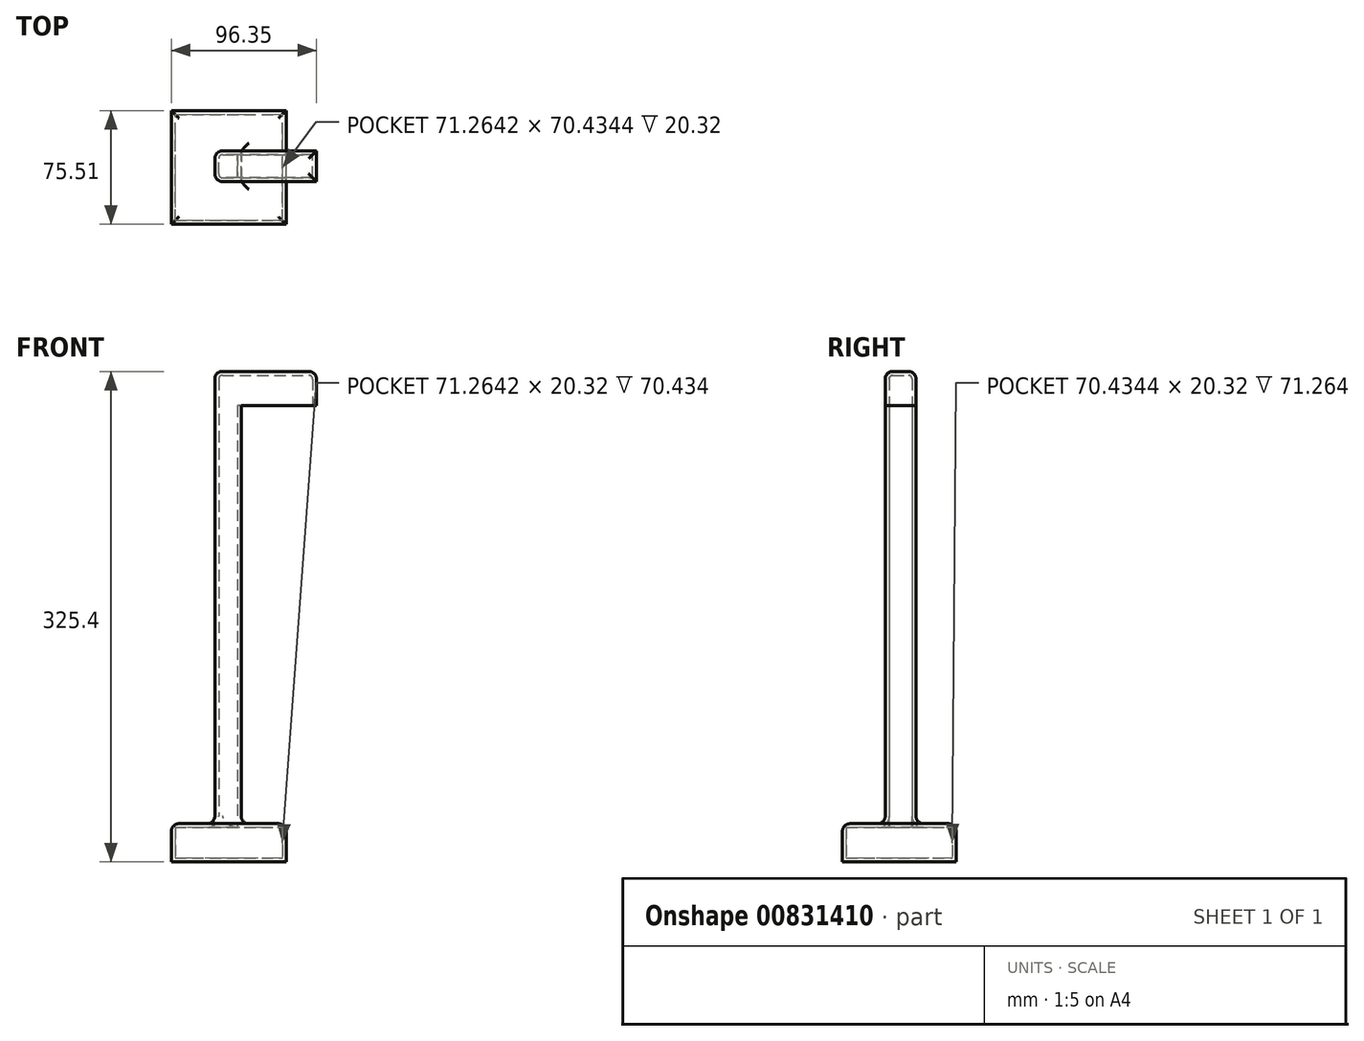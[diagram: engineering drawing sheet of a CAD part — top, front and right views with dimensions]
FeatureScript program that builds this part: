
annotation { "Feature Type Name" : "Feature", "Feature Type Description" : "" }
export const myFeature = defineFeature(function(context is Context, id is Id, definition is map)
    precondition{}
    {
        {
            var Q0;
            Q0=qCreatedBy(makeId("Top.planeOp"),FACE);
            var sketch = newSketch(context, id + "F0", { "sketchPlane" : qUnion([Q0])});
            skLineSegment(sketch, "E0.bottom", {"start": v(0, 0) * mm, "end": v(76.34, 0) * mm});
            skLineSegment(sketch, "E0.top", {"start": v(0, 75.51) * mm, "end": v(76.34, 75.51) * mm});
            skLineSegment(sketch, "E0.left", {"start": v(0, 0) * mm, "end": v(0, 75.51) * mm});
            skLineSegment(sketch, "E0.right", {"start": v(76.34, 0) * mm, "end": v(76.34, 75.51) * mm});
            skSolve(sketch);
        }
        {
            var Q0;
            Q0 = qSketchRegion(id + "F0", true);
            extrude(context, id + "F1", {"entities" : qUnion([Q0]), "depth" : 25.4 * mm, "offsetDistance" : 25.4 * mm});
        }
        {
            var Q0;
            Q0=makeQuery(id+"F1.opExtrude","CAP_FACE",FACE,{"disambiguationData":[OSD([sQuery(id+"F0.wireOp",EDGE,"E0.bottom"),sQuery(id+"F0.wireOp",EDGE,"E0.top"),sQuery(id+"F0.wireOp",EDGE,"E0.left"),sQuery(id+"F0.wireOp",EDGE,"E0.right")])],"isStart":false});
            var sketch = newSketch(context, id + "F2", { "sketchPlane" : qUnion([Q0])});
            skLineSegment(sketch, "E1.bottom", {"start": v(46.35, 48.77) * mm, "end": v(28.92, 48.77) * mm});
            skLineSegment(sketch, "E1.top", {"start": v(46.35, 28.43) * mm, "end": v(28.92, 28.43) * mm});
            skLineSegment(sketch, "E1.left", {"start": v(46.35, 48.77) * mm, "end": v(46.35, 28.43) * mm});
            skLineSegment(sketch, "E1.right", {"start": v(28.92, 48.77) * mm, "end": v(28.92, 28.43) * mm});
            skPoint(sketch, "E1.middle", {"position": v(37.63, 38.6) * mm});
            skSolve(sketch);
        }
        {
            var Q0;
            Q0=makeQuery(id+"F2.imprint","IMPRINT",FACE,{"disambiguationData":[TD([[makeQuery(id+"F2.imprint","IMPRINT",EDGE,{"derivedFrom":sQuery(id+"F2.wireOp",EDGE,"E1.bottom")}),1.0]])]});
            extrude(context, id + "F3", {"entities" : qUnion([Q0]), "operationType" : NewBodyOperationType.ADD, "depth" : 300 * mm, "offsetDistance" : 25.4 * mm});
        }
        {
            var Q0;
            Q0=makeQuery(id+"F3.opExtrude","SWEPT_FACE",FACE,{"disambiguationData":[OSD([sQuery(id+"F2.wireOp",EDGE,"E1.left")])]});
            var sketch = newSketch(context, id + "F4", { "sketchPlane" : qUnion([Q0])});
            skLineSegment(sketch, "E2.bottom", {"start": v(28.43, 325.4) * mm, "end": v(48.77, 325.4) * mm});
            skLineSegment(sketch, "E2.top", {"start": v(28.43, 302.61) * mm, "end": v(48.77, 302.61) * mm});
            skLineSegment(sketch, "E2.left", {"start": v(28.43, 325.4) * mm, "end": v(28.43, 302.61) * mm});
            skLineSegment(sketch, "E2.right", {"start": v(48.77, 325.4) * mm, "end": v(48.77, 302.61) * mm});
            skSolve(sketch);
        }
        {
            var Q0;
            Q0=makeQuery(id+"F4.imprint","IMPRINT",FACE,{"disambiguationData":[TD([[makeQuery(id+"F4.imprint","IMPRINT",EDGE,{"derivedFrom":sQuery(id+"F4.wireOp",EDGE,"E2.bottom")}),1.0]])]});
            extrude(context, id + "F5", {"entities" : qUnion([Q0]), "operationType" : NewBodyOperationType.ADD, "depth" : 50 * mm, "offsetDistance" : 25.4 * mm});
        }
        {
            var Q0;
            Q0=makeQuery(id+"F3.opExtrude","SWEPT_FACE",FACE,{"disambiguationData":[OSD([sQuery(id+"F2.wireOp",EDGE,"E1.right")])]});
            var Q1;
            Q1=makeQuery(id+"F5.boolean.opBoolean","MERGE",FACE,{"derivedFrom":[makeQuery(id+"F3.opExtrude","CAP_FACE",FACE,{"disambiguationData":[OSD([sQuery(id+"F2.wireOp",EDGE,"E1.bottom"),sQuery(id+"F2.wireOp",EDGE,"E1.top"),sQuery(id+"F2.wireOp",EDGE,"E1.left"),sQuery(id+"F2.wireOp",EDGE,"E1.right")])],"isStart":false}),makeQuery(id+"F5.opExtrude","SWEPT_FACE",FACE,{"disambiguationData":[OSD([sQuery(id+"F4.wireOp",EDGE,"E2.bottom")])]})]});
            fillet(context, id + "F6", {"entities" : qUnion([Q0, Q1]), "radius" : 5.08 * mm, "tangentPropagation" : true, "allowEdgeOverflow" : false});
        }
        {
            var Q0;
            Q0=makeQuery(id+"F5.opExtrude","SWEPT_FACE",FACE,{"disambiguationData":[OSD([sQuery(id+"F4.wireOp",EDGE,"E2.top")])]});
            shell(context, id + "F7", {"entities" : qUnion([Q0]), "thickness" : 2.54 * mm});
        }
        {
            var Q0;
            Q0=makeQuery(id+"F1.opExtrude","CAP_FACE",FACE,{"disambiguationData":[OSD([sQuery(id+"F0.wireOp",EDGE,"E0.bottom"),sQuery(id+"F0.wireOp",EDGE,"E0.top"),sQuery(id+"F0.wireOp",EDGE,"E0.left"),sQuery(id+"F0.wireOp",EDGE,"E0.right")])],"isStart":false});
            fillet(context, id + "F8", {"entities" : qUnion([Q0]), "radius" : 5.08 * mm, "tangentPropagation" : true, "allowEdgeOverflow" : false});
        }
    });
